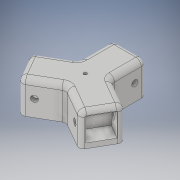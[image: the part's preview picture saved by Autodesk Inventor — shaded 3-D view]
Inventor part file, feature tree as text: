
AUTODESK INVENTOR PART (.ipt)
format: ipt  version: 2019.4 (Build 234330000, 330)  size: 229,888 bytes
history: native  units: mm
features: extrude x4, sketch x4, pattern_circular x3, fillet x3
ambient origin geometry x8: Origin, YZ Plane, XZ Plane, XY Plane, X Axis, Y Axis, Z Axis, Center Point
bodies: Solid1 (feature_tree)
feature tree (14):
  extrude  "Extrusion1"  Depth=40.0mm
  extrude  "Extrusion6"  Depth=30.0mm
  pattern_circular  "Circular Pattern4"  Count=3  [1 undecoded]
  extrude  "Extrusion7"  Depth=21.0mm
  pattern_circular  "Circular Pattern5"  [2 undecoded]
  extrude  "Extrusion8"  Depth=30.0mm TaperAngle=360.0deg
  pattern_circular  "Circular Pattern6"  [2 undecoded]
  fillet  "Fillet5"  Radius=5.5mm
  fillet  "Fillet6"  Radius=30.0mm
  fillet  "Fillet7"  Radius=30.0mm
  sketch  "Sketch1"  dims[d0=30.0mm d1=40.0mm]
  sketch  "Sketch6"  dims[d2=30.0mm d3=0.0mm d32=3.0mm d33=30.0mm d34=0.0mm]
  sketch  "Sketch7"  dims[d35=30.0mm d36=360.0deg d38=21.0mm]
  sketch  "Sketch8"  dims[d39=21.0mm d40=15.0mm d41=0.0mm d42=30.0mm d43=360.0deg d45=10.0mm d46=5.5mm d47=30.0mm d48=0.0mm d49=30.0mm d50=360.0deg d52=5.0mm d53=5.0mm d54=4.0mm]
note: 5 required parameter values undecoded (feature->parameter linkage not recoverable at this tier; creation-order binding heuristic only, values carry confidence <= 0.55)
